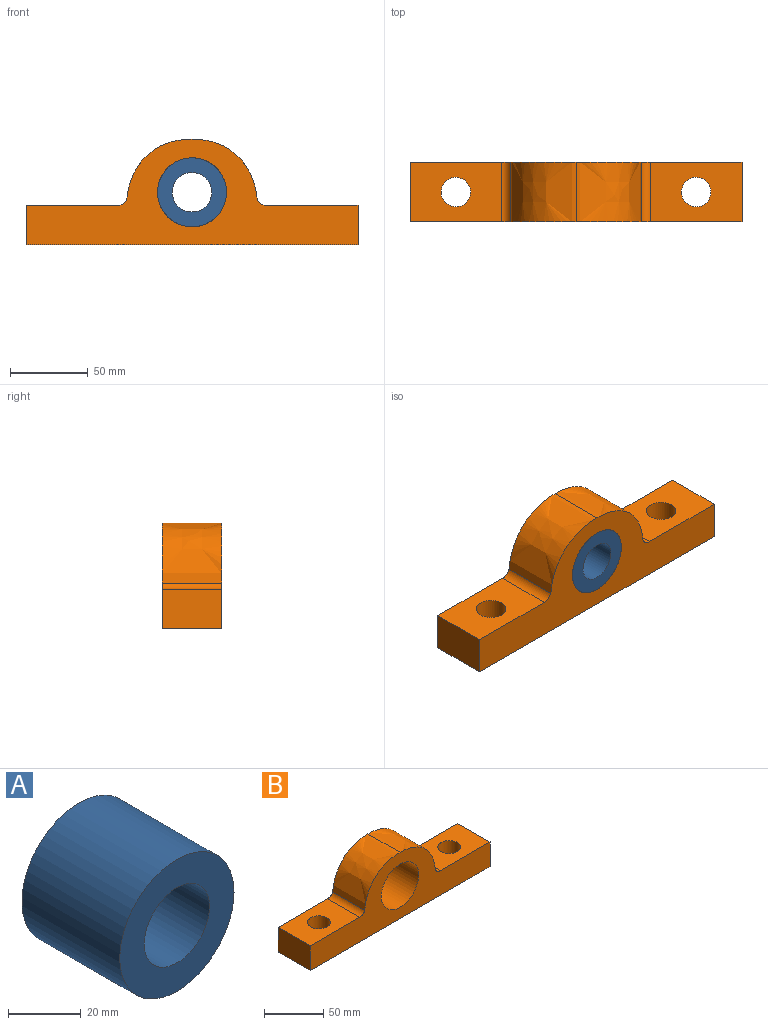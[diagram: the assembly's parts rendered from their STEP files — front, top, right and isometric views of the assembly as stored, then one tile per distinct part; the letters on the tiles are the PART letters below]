
ASSEMBLY  parts=2 mates=1
PART A: 4 faces, bbox 44.5x38.1x44.5 mm
  f0: cylinder r=12.7mm len=38.1mm, axis (0,1,0), area 3040.2mm2, adj f2,f3
  f1: cylinder r=22.23mm len=44.45mm, axis (0,1,0), area 5320.4mm2, adj f2,f3
  f2: plane 44.45x44.45mm, normal (0,-1,0), area 1045.1mm2, adj f0,f1
  f3: plane 44.45x44.45mm, normal (0,1,0), area 1045.1mm2, adj f0,f1
PART B: 14 faces, bbox 213.9x38.1x68.3 mm
  f0: plane 213.9x38.1mm, normal (0,0,-1), area 7579.5mm2, adj f1,f9,f10,f11,f12,f13
  f1: plane 38.1x25.4mm, normal (1,0,0), area 967.7mm2, adj f0,f2,f10,f11
  f2: plane 58.99x38.1mm, normal (0,0,1), area 1962.3mm2, adj f1,f3,f10,f11,f13
  f3: cylinder r=6.35mm len=38.1mm, axis (0,1,0), area 291.6mm2, adj f2,f4,f10,f11
  f4: extruded ~42.03x38.65mm, area 2412.9mm2, adj f3,f5,f10,f11
  f5: extruded ~42.03x38.65mm, area 2412.9mm2, adj f4,f6,f10,f11
  f6: cylinder r=6.35mm len=38.1mm, axis (0,1,0), area 291.6mm2, adj f5,f7,f10,f11
  f7: plane 58.99x38.1mm, normal (0,0,1), area 1962.3mm2, adj f6,f9,f10,f11,f12
  f8: cylinder r=22.23mm len=44.45mm, axis (0,1,0), area 5320.4mm2, adj f10,f11
  f9: plane 38.1x25.4mm, normal (-1,0,0), area 967.7mm2, adj f0,f7,f10,f11
  f10: plane 213.9x68.34mm, normal (0,-1,0), area 6784.4mm2, adj f0,f1,f2,f3,f4,f5,f6,f7
  f11: plane 213.9x68.34mm, normal (0,1,0), area 6784.4mm2, adj f0,f1,f2,f3,f4,f5,f6,f7
  f12: cylinder r=9.53mm len=25.4mm, axis (0,0,1), area 1520.1mm2, adj f0,f7
  f13: cylinder r=9.53mm len=25.4mm, axis (0,0,1), area 1520.1mm2, adj f0,f2
PLACE A rot(axis=(0,-1,0),26.6deg) t=(37.32,60.04,28.92)mm
PLACE B t=(37.32,60.04,-4.94)mm fixed
MATE revolute A.f0 <-> B.f8  axis (0,-1,0) through (37.32,21.94,28.92)mm
